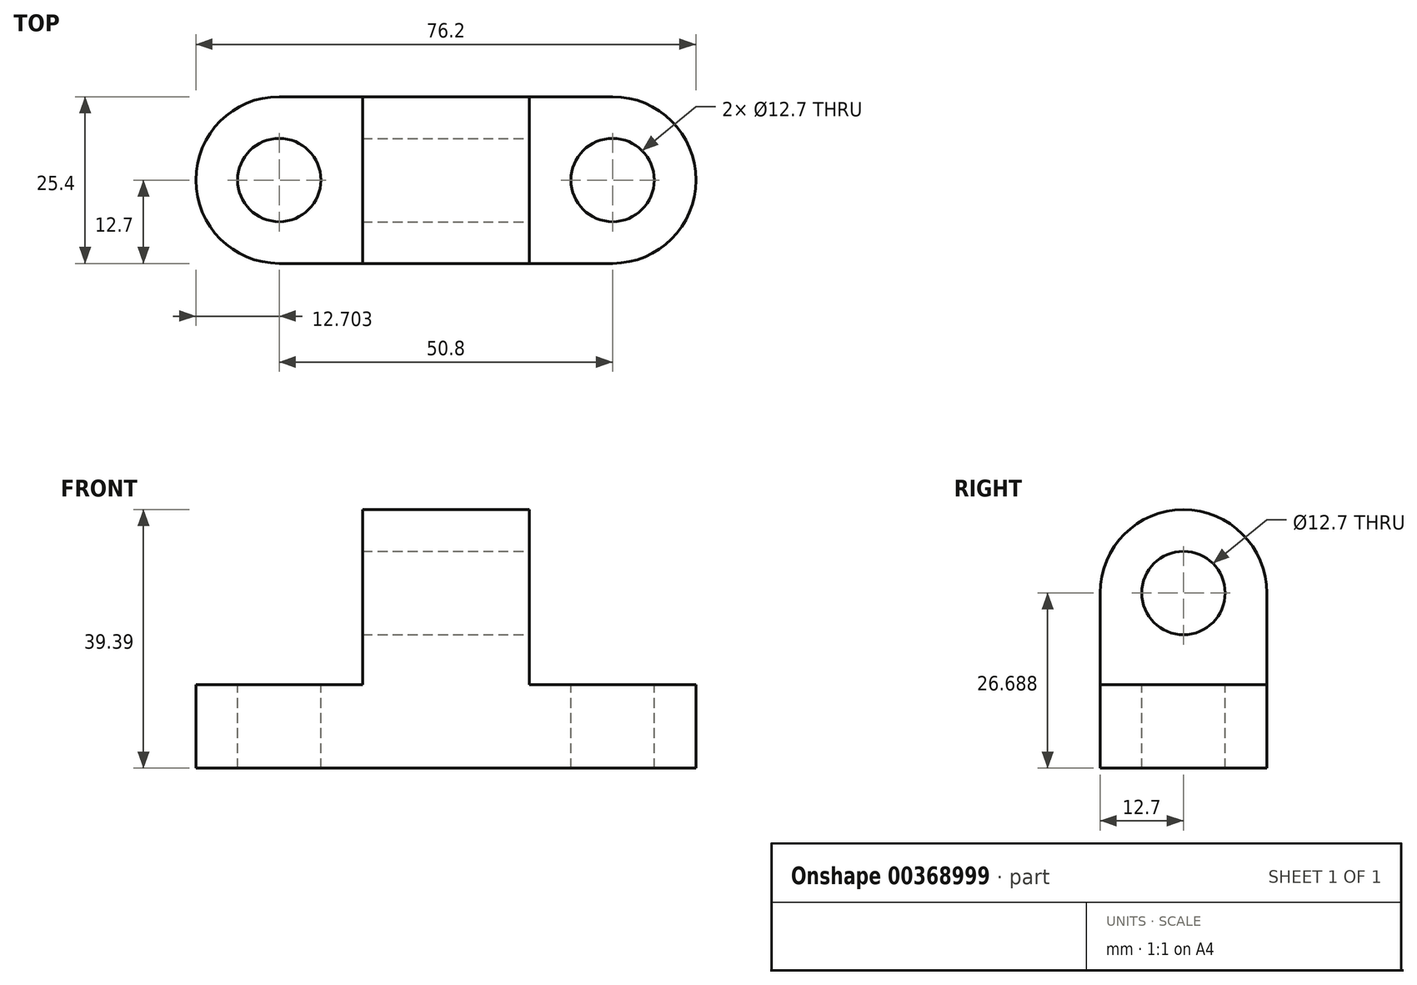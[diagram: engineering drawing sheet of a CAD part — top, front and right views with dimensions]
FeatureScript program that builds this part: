
annotation { "Feature Type Name" : "Feature", "Feature Type Description" : "" }
export const myFeature = defineFeature(function(context is Context, id is Id, definition is map)
    precondition{}
    {
        {
            var Q0;
            Q0=qCreatedBy(makeId("Front.planeOp"),FACE);
            var sketch = newSketch(context, id + "F0", { "sketchPlane" : qUnion([Q0])});
            skLineSegment(sketch, "E0", {"start": v(-49.98, -13.16) * mm, "end": v(26.22, -13.16) * mm});
            skLineSegment(sketch, "E1", {"start": v(26.22, -13.16) * mm, "end": v(26.22, -0.46) * mm});
            skLineSegment(sketch, "E2", {"start": v(26.22, -0.46) * mm, "end": v(0.82, -0.46) * mm});
            skLineSegment(sketch, "E3", {"start": v(0.82, -0.46) * mm, "end": v(0.82, 26.23) * mm});
            skLineSegment(sketch, "E4", {"start": v(0.82, 26.23) * mm, "end": v(-24.58, 26.23) * mm});
            skLineSegment(sketch, "E5", {"start": v(-24.58, 26.23) * mm, "end": v(-24.58, -0.46) * mm});
            skLineSegment(sketch, "E6", {"start": v(-24.58, -0.46) * mm, "end": v(-49.98, -0.46) * mm});
            skLineSegment(sketch, "E7", {"start": v(-49.98, -0.46) * mm, "end": v(-49.98, -13.16) * mm});
            skSolve(sketch);
        }
        {
            var Q0;
            Q0 = qSketchRegion(id + "F0", true);
            extrude(context, id + "F1", {"entities" : qUnion([Q0]), "depth" : 25.4 * mm});
        }
        {
            var Q0;
            Q0=makeQuery(id+"F1.opExtrude","SWEPT_FACE",FACE,{"disambiguationData":[OSD([sQuery(id+"F0.wireOp",EDGE,"E3")])]});
            var sketch = newSketch(context, id + "F2", { "sketchPlane" : qUnion([Q0])});
            skLineSegment(sketch, "E8", {"start": v(-25.4, -0.46) * mm, "end": v(-25.4, 13.53) * mm});
            skLineSegment(sketch, "E9", {"start": v(-12.7, 26.23) * mm, "end": v(-12.7, 26.23) * mm});
            skLineSegment(sketch, "E10", {"start": v(0, 13.53) * mm, "end": v(0, 0) * mm});
            skLineSegment(sketch, "E11", {"start": v(0, 0) * mm, "end": v(-25.4, -0.46) * mm});
            skPoint(sketch, "E12.visualSharp", {"position": v(-25.4, 26.23) * mm});
            skArc(sketch, "E12.filletArc", {"start": v(-12.7, 26.23) * mm, "mid": v(-21.68, 22.5) * mm, "end": v(-25.4, 13.53) * mm});
            skPoint(sketch, "E13.visualSharp", {"position": v(0, 26.23) * mm});
            skArc(sketch, "E13.filletArc", {"start": v(0, 13.53) * mm, "mid": v(-3.72, 22.5) * mm, "end": v(-12.7, 26.23) * mm});
            skSolve(sketch);
        }
        {
            var Q0;
            {var subQ0=sQuery(id+"F2.wireOp",EDGE,"E12.filletArc");Q0=makeQuery(id+"F2.imprint","IMPRINT",FACE,{"disambiguationData":[TD([[makeQuery(id+"F2.imprint","IMPRINT",EDGE,{"derivedFrom":subQ0}),-1.0]])]});}
            var Q1;
            {var subQ0=sQuery(id+"F2.wireOp",EDGE,"E13.filletArc");Q1=makeQuery(id+"F2.imprint","IMPRINT",FACE,{"disambiguationData":[TD([[makeQuery(id+"F2.imprint","IMPRINT",EDGE,{"derivedFrom":subQ0}),-1.0]])]});}
            extrude(context, id + "F3", {"entities" : qUnion([Q0, Q1]), "operationType" : NewBodyOperationType.REMOVE, "oppositeDirection" : true, "depth" : 25.4 * mm});
        }
        {
            var Q0;
            Q0=makeQuery(id+"F1.opExtrude","SWEPT_FACE",FACE,{"disambiguationData":[OSD([sQuery(id+"F0.wireOp",EDGE,"E2")])]});
            var sketch = newSketch(context, id + "F4", { "sketchPlane" : qUnion([Q0])});
            skLineSegment(sketch, "E14", {"start": v(0.82, 0) * mm, "end": v(13.52, 0) * mm});
            skLineSegment(sketch, "E15", {"start": v(26.22, -12.7) * mm, "end": v(26.22, -12.7) * mm});
            skLineSegment(sketch, "E16", {"start": v(13.52, -25.4) * mm, "end": v(0.82, -25.4) * mm});
            skLineSegment(sketch, "E17", {"start": v(0.82, -25.4) * mm, "end": v(0.82, 0) * mm});
            skPoint(sketch, "E18.visualSharp", {"position": v(26.22, 0) * mm});
            skArc(sketch, "E18.filletArc", {"start": v(26.22, -12.7) * mm, "mid": v(22.5, -3.72) * mm, "end": v(13.52, 0) * mm});
            skPoint(sketch, "E19.visualSharp", {"position": v(26.22, -25.4) * mm});
            skArc(sketch, "E19.filletArc", {"start": v(13.52, -25.4) * mm, "mid": v(22.5, -21.68) * mm, "end": v(26.22, -12.7) * mm});
            skSolve(sketch);
        }
        {
            var Q0;
            {var subQ0=sQuery(id+"F4.wireOp",EDGE,"E18.filletArc");Q0=makeQuery(id+"F4.imprint","IMPRINT",FACE,{"disambiguationData":[TD([[makeQuery(id+"F4.imprint","IMPRINT",EDGE,{"derivedFrom":subQ0}),-1.0]])]});}
            var Q1;
            {var subQ0=sQuery(id+"F4.wireOp",EDGE,"E19.filletArc");Q1=makeQuery(id+"F4.imprint","IMPRINT",FACE,{"disambiguationData":[TD([[makeQuery(id+"F4.imprint","IMPRINT",EDGE,{"derivedFrom":subQ0}),-1.0]])]});}
            extrude(context, id + "F5", {"entities" : qUnion([Q0, Q1]), "operationType" : NewBodyOperationType.REMOVE, "oppositeDirection" : true, "depth" : 25.4 * mm});
        }
        {
            var Q0;
            Q0=makeQuery(id+"F1.opExtrude","SWEPT_FACE",FACE,{"disambiguationData":[OSD([sQuery(id+"F0.wireOp",EDGE,"E6")])]});
            var sketch = newSketch(context, id + "F6", { "sketchPlane" : qUnion([Q0])});
            skLineSegment(sketch, "E20", {"start": v(-49.98, 0) * mm, "end": v(-24.58, 0) * mm});
            skLineSegment(sketch, "E21", {"start": v(-24.58, 0) * mm, "end": v(-24.58, -25.4) * mm});
            skLineSegment(sketch, "E22", {"start": v(-24.58, -25.4) * mm, "end": v(-37.28, -25.4) * mm});
            skLineSegment(sketch, "E23", {"start": v(-49.98, -12.7) * mm, "end": v(-49.98, 0) * mm});
            skPoint(sketch, "E24.visualSharp", {"position": v(-49.98, -25.4) * mm});
            skArc(sketch, "E24.filletArc", {"start": v(-49.98, -12.7) * mm, "mid": v(-46.26, -21.68) * mm, "end": v(-37.28, -25.4) * mm});
            skSolve(sketch);
        }
        {
            var Q0;
            {var subQ0=sQuery(id+"F6.wireOp",EDGE,"E24.filletArc");Q0=makeQuery(id+"F6.imprint","IMPRINT",FACE,{"disambiguationData":[TD([[makeQuery(id+"F6.imprint","IMPRINT",EDGE,{"derivedFrom":subQ0}),-1.0]])]});}
            extrude(context, id + "F7", {"entities" : qUnion([Q0]), "operationType" : NewBodyOperationType.REMOVE, "oppositeDirection" : true, "depth" : 25.4 * mm});
        }
        {
            var Q0;
            Q0=makeQuery(id+"F1.opExtrude","SWEPT_FACE",FACE,{"disambiguationData":[OSD([sQuery(id+"F0.wireOp",EDGE,"E6")])]});
            var sketch = newSketch(context, id + "F8", { "sketchPlane" : qUnion([Q0])});
            skLineSegment(sketch, "E25", {"start": v(-37.28, 0) * mm, "end": v(-24.58, 0) * mm});
            skLineSegment(sketch, "E26", {"start": v(-24.58, 0) * mm, "end": v(-24.58, -25.4) * mm});
            skLineSegment(sketch, "E27", {"start": v(-24.58, -25.4) * mm, "end": v(-49.98, -25.4) * mm});
            skLineSegment(sketch, "E28", {"start": v(-49.98, -12.7) * mm, "end": v(-49.98, -25.4) * mm});
            skPoint(sketch, "E29.visualSharp", {"position": v(-49.98, 0) * mm});
            skArc(sketch, "E29.filletArc", {"start": v(-37.28, 0) * mm, "mid": v(-46.26, -3.72) * mm, "end": v(-49.98, -12.7) * mm});
            skSolve(sketch);
        }
        {
            var Q0;
            {var subQ2=sQuery(id+"F8.wireOp",EDGE,"E28");Q0=makeQuery(id+"F8.imprint","IMPRINT",FACE,{"disambiguationData":[TD([[makeQuery(id+"F8.imprint","IMPRINT",EDGE,{"derivedFrom":subQ2}),1.0]])]});}
            var Q1;
            {var subQ0=sQuery(id+"F8.wireOp",EDGE,"E29.filletArc");Q1=makeQuery(id+"F8.imprint","IMPRINT",FACE,{"disambiguationData":[TD([[makeQuery(id+"F8.imprint","IMPRINT",EDGE,{"derivedFrom":subQ0}),-1.0]])]});}
            extrude(context, id + "F9", {"entities" : qUnion([Q0, Q1]), "operationType" : NewBodyOperationType.REMOVE, "oppositeDirection" : true, "depth" : 25.4 * mm});
        }
        {
            var Q0;
            Q0=makeQuery(id+"F1.opExtrude","SWEPT_FACE",FACE,{"disambiguationData":[OSD([sQuery(id+"F0.wireOp",EDGE,"E6")])]});
            var sketch = newSketch(context, id + "F10", { "sketchPlane" : qUnion([Q0])});
            skCircle(sketch, "E30", {"center": v(-37.28, -12.7) * mm, "radius": 6.35 * mm});
            skLineSegment(sketch, "E31", {"start": v(-37.28, -12.7) * mm, "end": v(-37.28, -6.35) * mm});
            skSolve(sketch);
        }
        {
            var Q0;
            Q0=makeQuery(id+"F10.imprint","IMPRINT",FACE,{"disambiguationData":[TD([[makeQuery(id+"F10.imprint","IMPRINT",EDGE,{"derivedFrom":sQuery(id+"F10.wireOp",EDGE,"E30")}),1.0]])]});
            extrude(context, id + "F11", {"entities" : qUnion([Q0]), "operationType" : NewBodyOperationType.REMOVE, "oppositeDirection" : true, "depth" : 25.4 * mm});
        }
        {
            var Q0;
            Q0=makeQuery(id+"F1.opExtrude","SWEPT_FACE",FACE,{"disambiguationData":[OSD([sQuery(id+"F0.wireOp",EDGE,"E2")])]});
            var sketch = newSketch(context, id + "F12", { "sketchPlane" : qUnion([Q0])});
            skCircle(sketch, "E32", {"center": v(13.52, -12.7) * mm, "radius": 6.35 * mm});
            skLineSegment(sketch, "E33", {"start": v(13.52, -12.7) * mm, "end": v(13.52, -6.35) * mm});
            skSolve(sketch);
        }
        {
            var Q0;
            Q0=makeQuery(id+"F12.imprint","IMPRINT",FACE,{"disambiguationData":[TD([[makeQuery(id+"F12.imprint","IMPRINT",EDGE,{"derivedFrom":sQuery(id+"F12.wireOp",EDGE,"E32")}),1.0]])]});
            extrude(context, id + "F13", {"entities" : qUnion([Q0]), "operationType" : NewBodyOperationType.REMOVE, "oppositeDirection" : true, "depth" : 25.4 * mm});
        }
        {
            var Q0;
            Q0=makeQuery(id+"F1.opExtrude","SWEPT_FACE",FACE,{"disambiguationData":[OSD([sQuery(id+"F0.wireOp",EDGE,"E3")])]});
            var sketch = newSketch(context, id + "F14", { "sketchPlane" : qUnion([Q0])});
            skCircle(sketch, "E34", {"center": v(-12.7, 13.53) * mm, "radius": 6.35 * mm});
            skLineSegment(sketch, "E35", {"start": v(-12.8, 19.88) * mm, "end": v(-12.7, 13.53) * mm});
            skSolve(sketch);
        }
        {
            var Q0;
            Q0=makeQuery(id+"F14.imprint","IMPRINT",FACE,{"disambiguationData":[TD([[makeQuery(id+"F14.imprint","IMPRINT",EDGE,{"derivedFrom":sQuery(id+"F14.wireOp",EDGE,"E34")}),1.0]])]});
            extrude(context, id + "F15", {"entities" : qUnion([Q0]), "operationType" : NewBodyOperationType.REMOVE, "oppositeDirection" : true, "depth" : 25.4 * mm});
        }
    });
